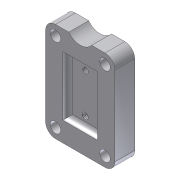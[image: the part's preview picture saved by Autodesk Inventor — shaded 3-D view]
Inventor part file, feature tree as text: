
AUTODESK INVENTOR PART (.ipt)
format: ipt  version: unknown  size: 230,400 bytes
history: native  units: mm (DEFAULTED — no unit token found)
features: sketch x5, extrude x3, hole x2, fillet x2, projected_geometry x2, plane x1, mirror x1
ambient origin geometry x8: Origin, YZ Plane, XZ Plane, XY Plane, X Axis, Y Axis, Z Axis, Center Point
feature tree (16):
  extrude  "Extrusion1"  Depth=63.5mm
  hole  "Hole1"  [1 undecoded]
  fillet  "Fillet1"  Radius=6.35mm
  extrude  "Extrusion2"  Depth=6.35mm
  fillet  "Fillet2"  Radius=6.35mm
  hole  "Hole2"  [1 undecoded]
  plane  "Work Plane1"
  mirror  "Mirror1"
  extrude  "Extrusion3"  Depth=12.7mm
  sketch  "Sketch1"  dims[d0=44.45mm d1=63.5mm]
  sketch  "Sketch2"  dims[d2=12.7mm d3=0.0mm d4=6.35mm d5=6.35mm]
  projected_geometry  "Projected Loop1"
  sketch  "Sketch3"  dims[d6=6.35mm d7=6.35mm]
  sketch  "Sketch4"  dims[d8=6.731mm d9=12.7mm d10=9.525mm d11=6.35mm d12=14.3117mm d13=19.05mm d14=20.594885mm d15=6.35mm]
  projected_geometry  "Projected Loop2"
  sketch  "Sketch5"  dims[d16=11.0998mm d17=22.225mm d18=12.7mm d19=38.1mm d20=3.175mm d21=0.0mm d22=3.175mm d23=15.875mm d24=12.7mm d25=3.9624mm d26=12.7mm d27=9.525mm d28=6.35mm d29=14.3117mm d30=19.05mm d31=20.594885mm d32=-31.75mm d33=25.4mm d34=0.0mm d35=0.0mm d36=0.0mm d37=0.0mm d38=0.0mm]
note: 2 required parameter values undecoded (feature->parameter linkage not recoverable at this tier; creation-order binding heuristic only, values carry confidence <= 0.55)
